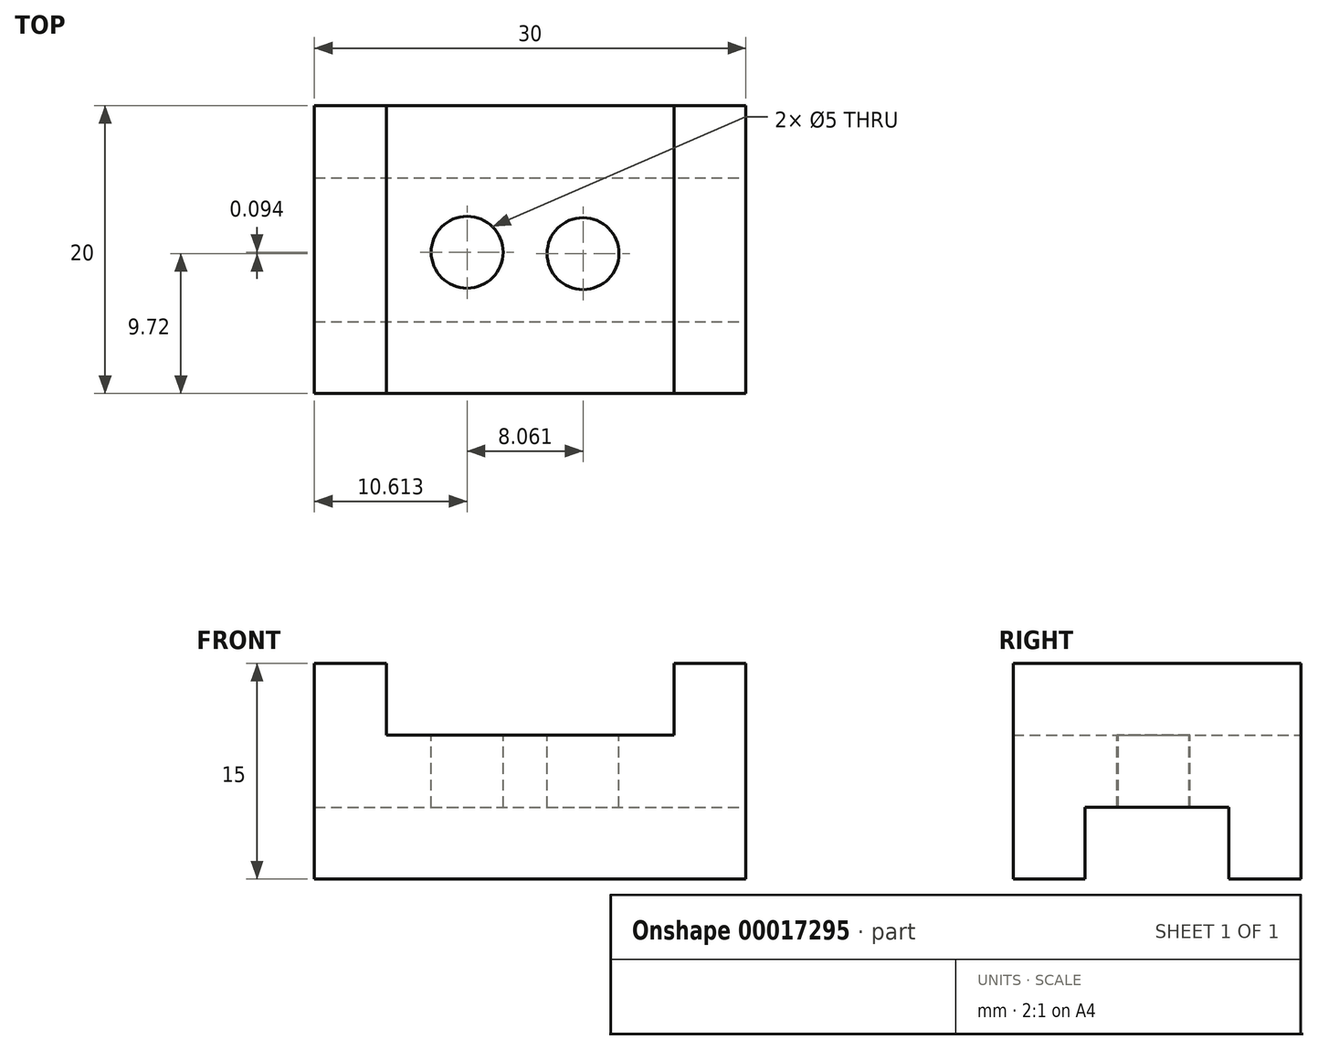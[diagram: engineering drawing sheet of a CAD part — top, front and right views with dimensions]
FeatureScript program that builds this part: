
annotation { "Feature Type Name" : "Feature", "Feature Type Description" : "" }
export const myFeature = defineFeature(function(context is Context, id is Id, definition is map)
    precondition{}
    {
        {
            var Q0;
            Q0=qCreatedBy(makeId("Front.planeOp"),FACE);
            var sketch = newSketch(context, id + "F0", { "sketchPlane" : qUnion([Q0])});
            skLineSegment(sketch, "E0", {"start": v(0, 0) * mm, "end": v(0, 15) * mm});
            skLineSegment(sketch, "E1", {"start": v(0, 15) * mm, "end": v(-5, 15) * mm});
            skLineSegment(sketch, "E2", {"start": v(-5, 15) * mm, "end": v(-5, 10) * mm});
            skLineSegment(sketch, "E3", {"start": v(-5, 10) * mm, "end": v(-25, 10) * mm});
            skLineSegment(sketch, "E4", {"start": v(-25, 10) * mm, "end": v(-25, 15) * mm});
            skLineSegment(sketch, "E5", {"start": v(-25, 15) * mm, "end": v(-30, 15) * mm});
            skLineSegment(sketch, "E6", {"start": v(-30, 15) * mm, "end": v(-30, 0) * mm});
            skLineSegment(sketch, "E7", {"start": v(-30, 0) * mm, "end": v(0, 0) * mm});
            skSolve(sketch);
        }
        {
            var Q0;
            Q0=makeQuery(id+"F0.imprint","IMPRINT",FACE,{"disambiguationData":[TD([[makeQuery(id+"F0.imprint","IMPRINT",EDGE,{"derivedFrom":sQuery(id+"F0.wireOp",EDGE,"E0")}),1.0]])]});
            extrude(context, id + "F1", {"entities" : qUnion([Q0]), "depth" : 20 * mm});
        }
        {
            var Q0;
            Q0=makeQuery(id+"F1.opExtrude","SWEPT_FACE",FACE,{"disambiguationData":[OSD([sQuery(id+"F0.wireOp",EDGE,"E3")])]});
            var sketch = newSketch(context, id + "F2", { "sketchPlane" : qUnion([Q0])});
            skCircle(sketch, "E8", {"center": v(-19.39, -10.19) * mm, "radius": 2.5 * mm});
            skCircle(sketch, "E9", {"center": v(-11.33, -10.28) * mm, "radius": 2.5 * mm});
            skSolve(sketch);
        }
        {
            var Q0;
            Q0=makeQuery(id+"F2.imprint","IMPRINT",FACE,{"disambiguationData":[TD([[makeQuery(id+"F2.imprint","IMPRINT",EDGE,{"derivedFrom":sQuery(id+"F2.wireOp",EDGE,"E8")}),1.0]])]});
            var Q1;
            Q1=makeQuery(id+"F2.imprint","IMPRINT",FACE,{"disambiguationData":[TD([[makeQuery(id+"F2.imprint","IMPRINT",EDGE,{"derivedFrom":sQuery(id+"F2.wireOp",EDGE,"E9")}),1.0]])]});
            extrude(context, id + "F3", {"entities" : qUnion([Q0, Q1]), "operationType" : NewBodyOperationType.REMOVE, "oppositeDirection" : true, "depth" : 25 * mm});
        }
        {
            var Q0;
            Q0=makeQuery(id+"F1.opExtrude","SWEPT_FACE",FACE,{"disambiguationData":[OSD([sQuery(id+"F0.wireOp",EDGE,"E0")])]});
            var sketch = newSketch(context, id + "F4", { "sketchPlane" : qUnion([Q0])});
            skLineSegment(sketch, "E10", {"start": v(-15, 0) * mm, "end": v(-15, 5) * mm});
            skLineSegment(sketch, "E11", {"start": v(-15, 5) * mm, "end": v(-5, 5) * mm});
            skLineSegment(sketch, "E12", {"start": v(-5, 5) * mm, "end": v(-5, 0) * mm});
            skLineSegment(sketch, "E13", {"start": v(-5, 0) * mm, "end": v(-15, 0) * mm});
            skLineSegment(sketch, "E14", {"start": v(-20, 0) * mm, "end": v(-15, 0) * mm});
            skSolve(sketch);
        }
        {
            var Q0;
            Q0=makeQuery(id+"F4.imprint","IMPRINT",FACE,{"disambiguationData":[TD([[makeQuery(id+"F4.imprint","IMPRINT",EDGE,{"derivedFrom":sQuery(id+"F4.wireOp",EDGE,"E10")}),-1.0]])]});
            extrude(context, id + "F5", {"entities" : qUnion([Q0]), "operationType" : NewBodyOperationType.REMOVE, "oppositeDirection" : true, "depth" : 30 * mm});
        }
    });
